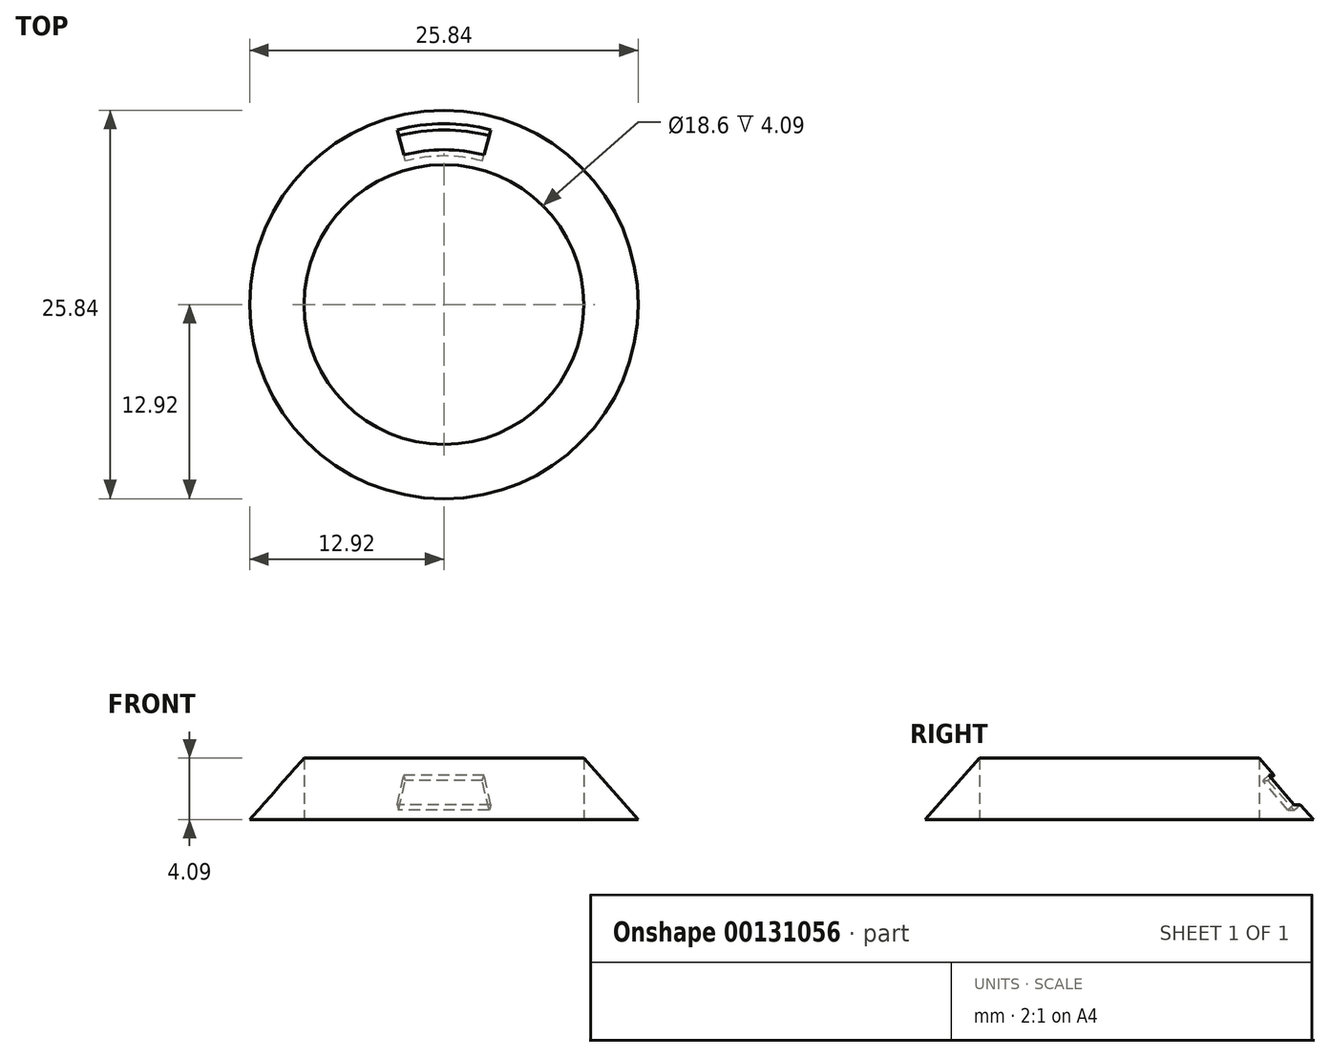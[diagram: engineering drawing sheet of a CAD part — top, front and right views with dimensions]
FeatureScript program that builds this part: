
annotation { "Feature Type Name" : "Feature", "Feature Type Description" : "" }
export const myFeature = defineFeature(function(context is Context, id is Id, definition is map)
    precondition{}
    {
        {
            var Q0;
            Q0=qCreatedBy(makeId("Right.planeOp"),FACE);
            var sketch = newSketch(context, id + "F0", { "sketchPlane" : qUnion([Q0])});
            skLineSegment(sketch, "E0", {"start": v(0, 0) * mm, "end": v(9.3, 0) * mm, "construction": true});
            skLineSegment(sketch, "E1", {"start": v(9.3, 0) * mm, "end": v(12.92, 0) * mm});
            skLineSegment(sketch, "E2", {"start": v(12.92, 0) * mm, "end": v(9.3, 4.09) * mm});
            skLineSegment(sketch, "E3", {"start": v(9.3, 4.09) * mm, "end": v(9.3, 0) * mm});
            skLineSegment(sketch, "E4", {"start": v(0, 0) * mm, "end": v(0, 4.36) * mm, "construction": true});
            skLineSegment(sketch, "E5", {"start": v(12.04, 1) * mm, "end": v(11.62, 0.63) * mm});
            skLineSegment(sketch, "E6", {"start": v(11.62, 0.63) * mm, "end": v(9.89, 2.59) * mm});
            skLineSegment(sketch, "E7", {"start": v(9.89, 2.59) * mm, "end": v(10.3, 2.96) * mm});
            skSolve(sketch);
        }
        {
            var Q0;
            Q0=makeQuery(id+"F0.imprint","IMPRINT",FACE,{"disambiguationData":[TD([[makeQuery(id+"F0.imprint","IMPRINT",EDGE,{"derivedFrom":sQuery(id+"F0.wireOp",EDGE,"E1")}),1.0]])]});
            var Q1;
            {var subQ0=sQuery(id+"F0.wireOp",EDGE,"E5");Q1=makeQuery(id+"F0.imprint","IMPRINT",FACE,{"disambiguationData":[TD([[makeQuery(id+"F0.imprint","IMPRINT",EDGE,{"derivedFrom":subQ0}),-1.0]])]});}
            var Q2;
            Q2=sQuery(id+"F0.wireOp",EDGE,"E4");
            revolve(context, id + "F1", {"entities" : qUnion([Q0, Q1]), "axis" : qUnion([Q2]), "revolveType" : RevolveType.FULL});
        }
        {
            var Q0;
            {var subQ0=sQuery(id+"F0.wireOp",EDGE,"E5");Q0=makeQuery(id+"F0.imprint","IMPRINT",FACE,{"disambiguationData":[TD([[makeQuery(id+"F0.imprint","IMPRINT",EDGE,{"derivedFrom":subQ0}),-1.0]])]});}
            var Q1;
            Q1=sQuery(id+"F0.wireOp",EDGE,"E4");
            revolve(context, id + "F2", {"operationType" : NewBodyOperationType.REMOVE, "entities" : qUnion([Q0]), "axis" : qUnion([Q1]), "revolveType" : RevolveType.SYMMETRIC, "oppositeDirection" : true, "angle" : 30 * degree});
        }
    });
